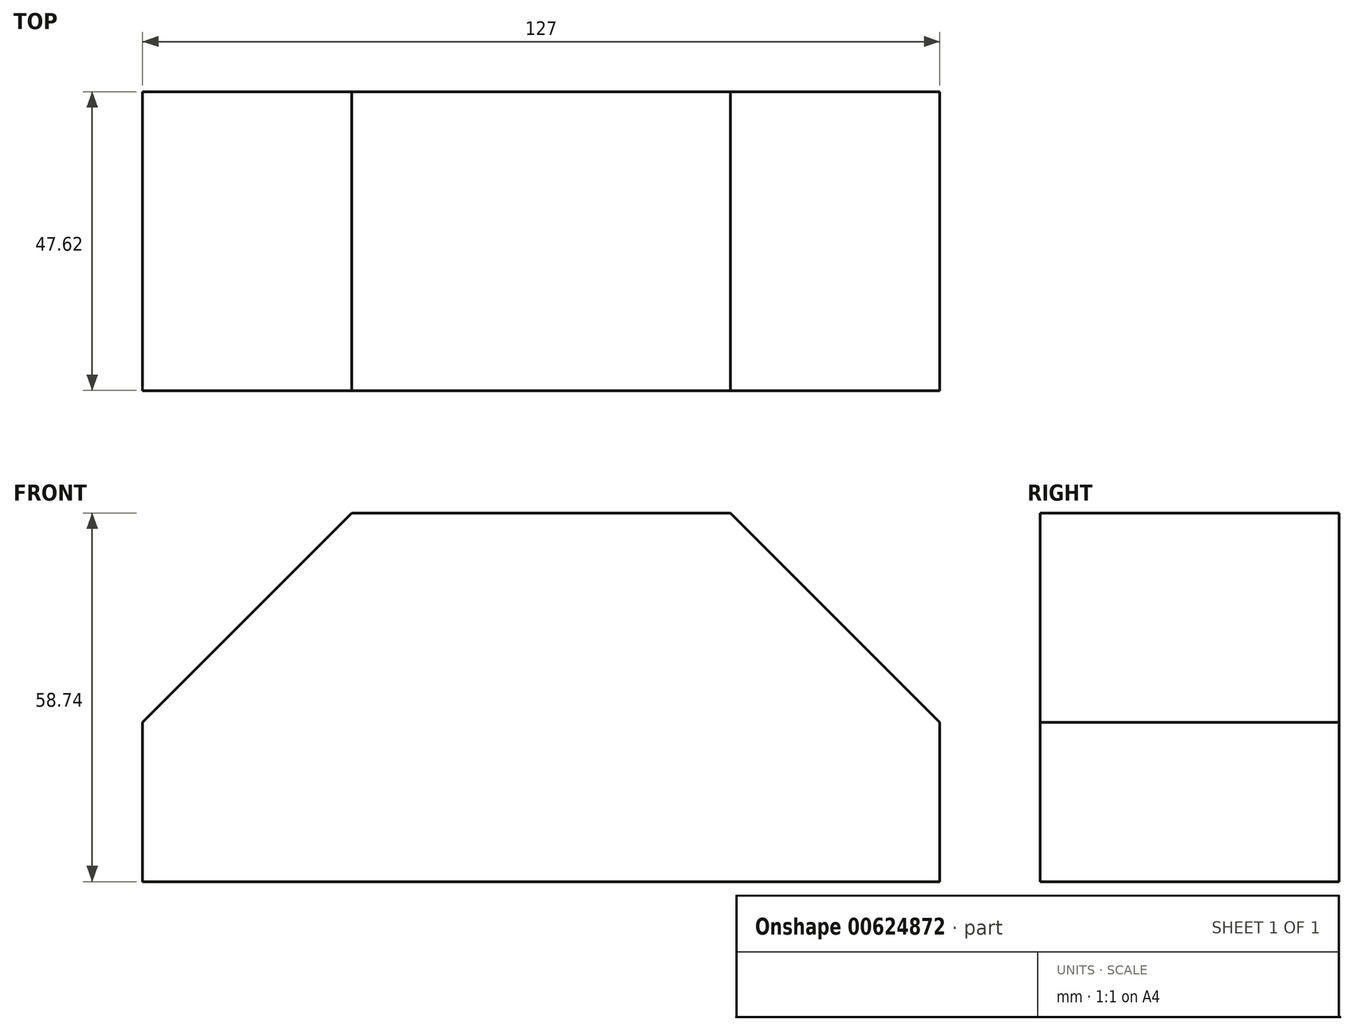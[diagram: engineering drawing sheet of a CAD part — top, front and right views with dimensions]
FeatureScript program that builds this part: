
annotation { "Feature Type Name" : "Feature", "Feature Type Description" : "" }
export const myFeature = defineFeature(function(context is Context, id is Id, definition is map)
    precondition{}
    {
        {
            var Q0;
            Q0=qCreatedBy(makeId("Front.planeOp"),FACE);
            var sketch = newSketch(context, id + "F0", { "sketchPlane" : qUnion([Q0])});
            skLineSegment(sketch, "E0.top", {"start": v(-63.5, -29.37) * mm, "end": v(63.5, -29.37) * mm});
            skPoint(sketch, "E0.middle", {"position": v(0, 0) * mm});
            skLineSegment(sketch, "E1", {"start": v(-63.5, -3.97) * mm, "end": v(-30.16, 29.37) * mm});
            skLineSegment(sketch, "E2", {"start": v(-63.5, -3.97) * mm, "end": v(-63.5, -29.37) * mm});
            skLineSegment(sketch, "E3", {"start": v(30.16, 29.37) * mm, "end": v(63.5, -3.97) * mm});
            skLineSegment(sketch, "E4", {"start": v(-30.16, 29.37) * mm, "end": v(30.16, 29.37) * mm});
            skLineSegment(sketch, "E5", {"start": v(63.5, -3.97) * mm, "end": v(63.5, -29.37) * mm});
            skSolve(sketch);
        }
        {
            var Q0;
            Q0=makeQuery(id+"F0.imprint","IMPRINT",FACE,{"disambiguationData":[TD([[makeQuery(id+"F0.imprint","IMPRINT",EDGE,{"derivedFrom":sQuery(id+"F0.wireOp",EDGE,"E0.top")}),1.0]])]});
            extrude(context, id + "F1", {"entities" : qUnion([Q0]), "depth" : 47.62 * mm, "offsetDistance" : 25.4 * mm});
        }
    });
